# Revit family: Deca_Misturador monocomando de mesa com filtro para cozinha_Filtro Cozinha Médio_2240
name_source: partatom
category: Plumbing Fixtures
units: mm (PartAtom-declared; Revit-internal decimal feet)

## family parameters
Cut with Voids When Loaded = No
Host = Face
Part Type = Normal
Room Calculation Point = No
Round Connector Dimension = Use Radius
Shared = No

## types (4) — shared parameters
Acompanha o Produto = Acompanha Ligação flexivel
Aprovado por = quattroD
Atendimento ao Cliente = 0800-0117073
Categoria = FILTROS
Composição Anel Vedação = -
Composição Assento = -
Composição Básica = Liga de Cobre (bronze e latão),Plásticos de Engenharia,Elastômeros
Composição Componente = -
Consumo = -
Cor Interna = -
Cor Secundária = -
Cores Componente = -
Criado por = quattroD
Código Pai = 2240
Description = Misturador monocomando de mesa com filtro para cozinha
Diâmetro Água Fria = 0.02 m
Diâmetro Água Quente = 0.02 m
Informações Complementares = -
Itens de Instalação = -
Linha = Filtro Cozinha Médio
Manufacturer = Deca
Norma = NBR16098
Pressão máx. funcionamento = 40 MCA
Pressão mín. Aquec. Acúmulo = 2 MCA
Pressão mín. Aquec. Passagem = 10 MCA
Pressão mín. funcionamento = 2 MCA
Raio Água Fria = 0.01 m
Raio Água Quente = 0.01 m
Saída de Esgoto = -
Segmento = Banheiro Médio
Tipo de dispositivo economizador = Não
Tipo de mecanismo utilizado = Cartucho Monocomando
Tipo de rosca de entrada = BSP NBR 8133
URL = www.deca.com.br
Vazão na Pressão máx. (L/min) = 15
Vazão na Pressão mín. (L/min) = 4
zero-valued in all types: CWFU, Default Elevation, HWFU

## per-type parameters (varying)
| type | Cor Principal | Material | Model | Peso Líquido (Kg) | Tipo de rosca de saída |
| 2240.BL.MT_Black Matte | Black Matte | Deca_Black Matte | 2240.BL.MT | 3.495 | - |
| 2240.C_Cromado | Cromado | Deca_Cromado | 2240.C | 3.364 | - |
| 2240.CT.MT_Corten | Corten | Deca_Corten | 2240.CT.MT | 3.492 | BSP NBR 8133 |
| 2240.GL.RD_Red Gold | Red Gold | Deca_Red Gold | 2240.GL.RD | 3.364 | BSP NBR 8133 |

note: source unit labels omitted for Vazão na Pressão máx. (L/min), Vazão na Pressão mín. (L/min) — the stored unit's dimension contradicts the parameter name (converter mislabeling)

## geometry (parser evidence)
native form markers: Sweep x3
no freeform markers — native parametric forms only
